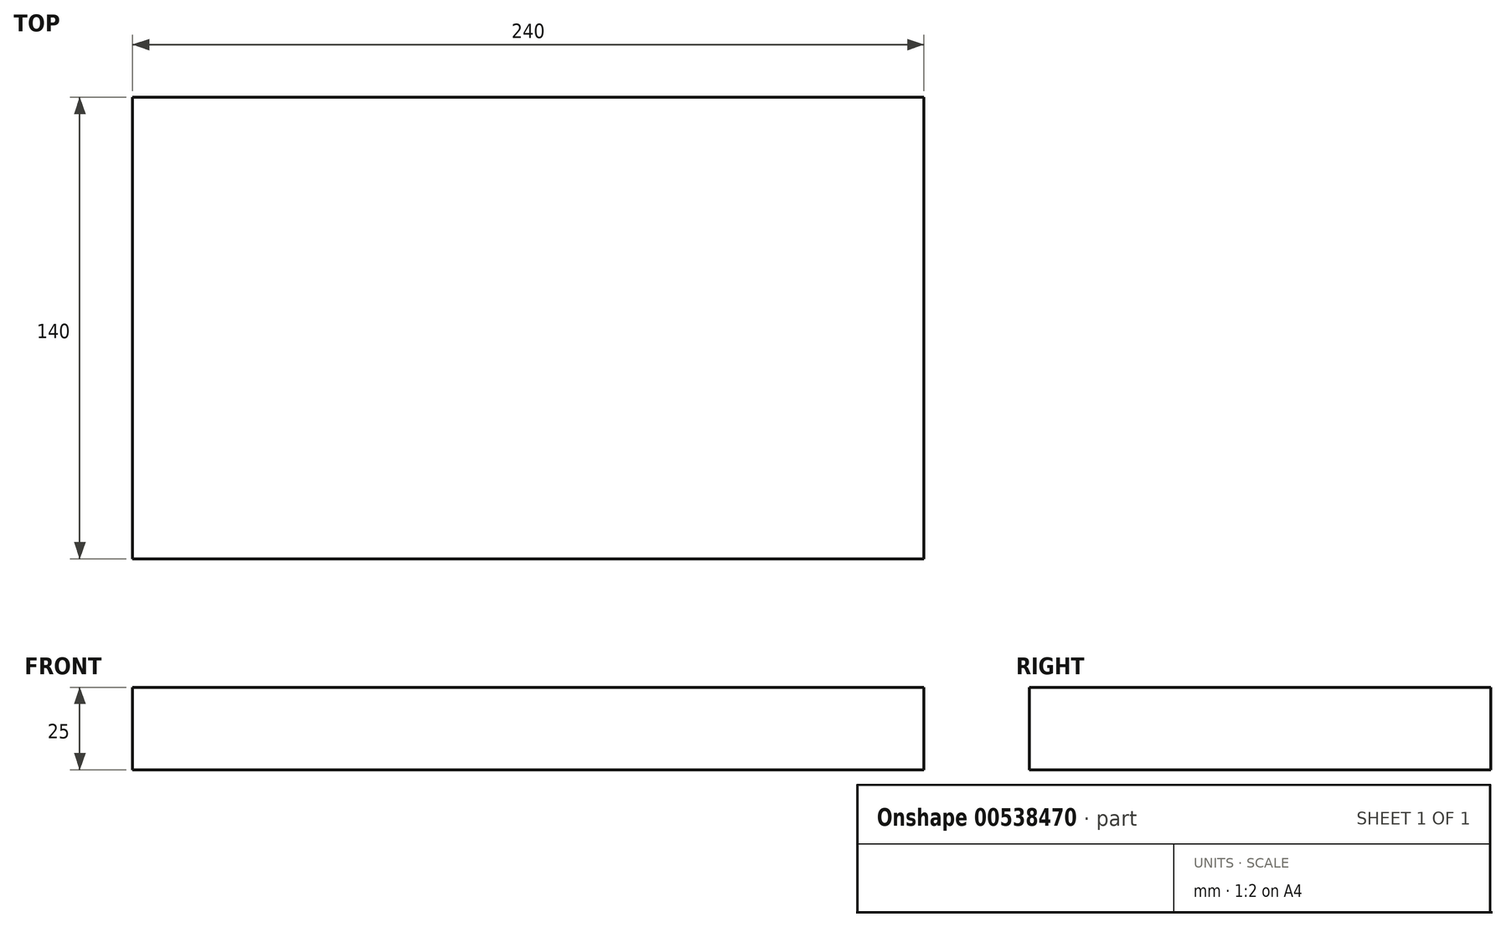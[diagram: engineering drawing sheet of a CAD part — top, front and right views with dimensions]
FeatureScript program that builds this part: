
annotation { "Feature Type Name" : "Feature", "Feature Type Description" : "" }
export const myFeature = defineFeature(function(context is Context, id is Id, definition is map)
    precondition{}
    {
        {
            var Q0;
            Q0=qCreatedBy(makeId("Top.planeOp"),FACE);
            var sketch = newSketch(context, id + "F0", { "sketchPlane" : qUnion([Q0])});
            skLineSegment(sketch, "E0.bottom", {"start": v(120, -70) * mm, "end": v(-120, -70) * mm});
            skLineSegment(sketch, "E0.top", {"start": v(120, 70) * mm, "end": v(-120, 70) * mm});
            skLineSegment(sketch, "E0.left", {"start": v(120, -70) * mm, "end": v(120, 70) * mm});
            skLineSegment(sketch, "E0.right", {"start": v(-120, -70) * mm, "end": v(-120, 70) * mm});
            skPoint(sketch, "E0.middle", {"position": v(0, 0) * mm});
            skSolve(sketch);
        }
        {
            var Q0;
            Q0 = qSketchRegion(id + "F0", true);
            extrude(context, id + "F1", {"entities" : qUnion([Q0]), "depth" : 25 * mm, "offsetDistance" : 25 * mm});
        }
    });
